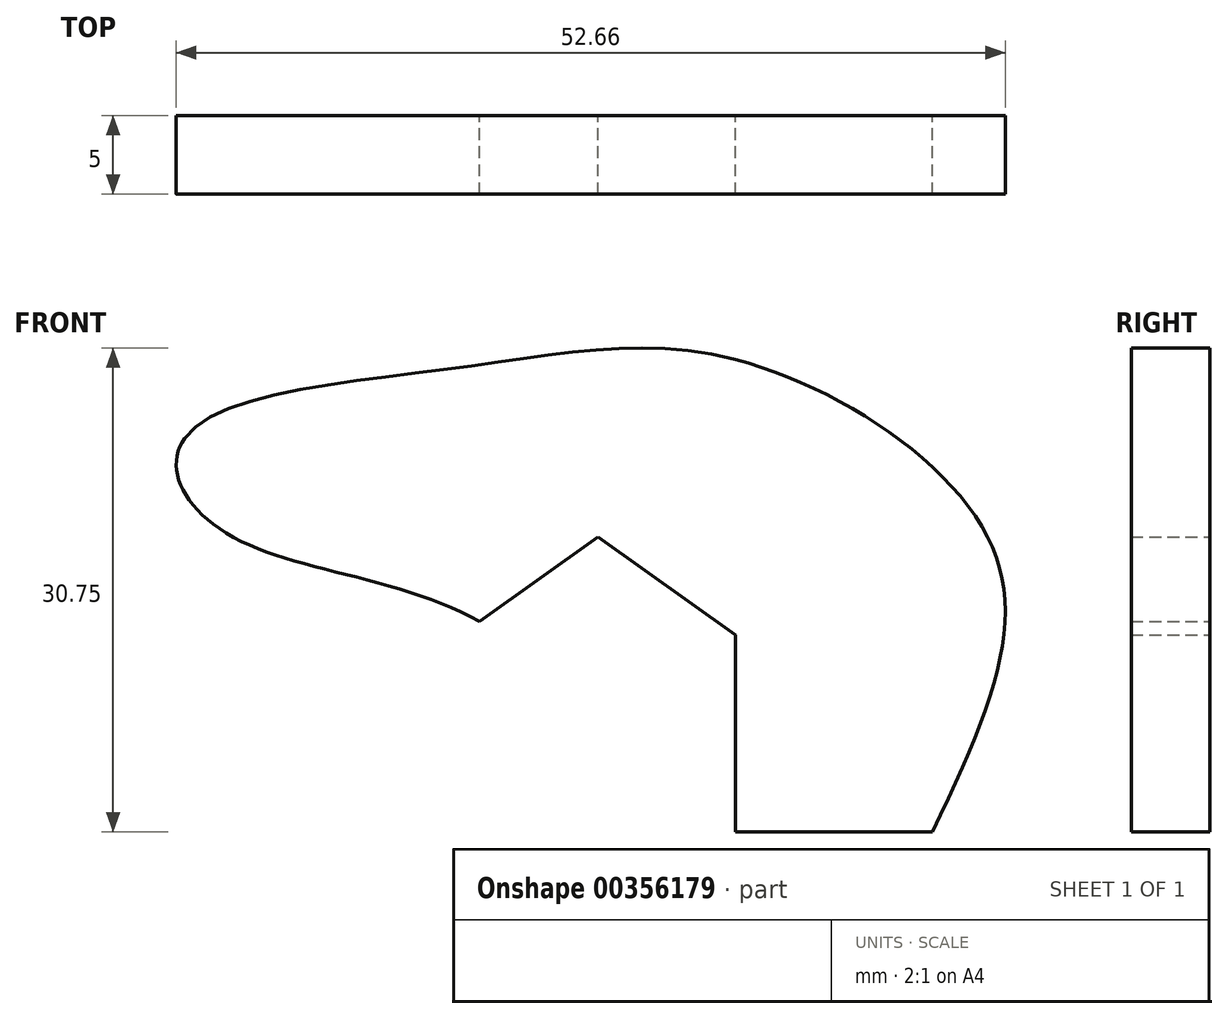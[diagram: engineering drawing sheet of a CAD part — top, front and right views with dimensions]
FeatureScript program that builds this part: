
annotation { "Feature Type Name" : "Feature", "Feature Type Description" : "" }
export const myFeature = defineFeature(function(context is Context, id is Id, definition is map)
    precondition{}
    {
        {
            var Q0;
            Q0=qCreatedBy(makeId("Front.planeOp"),FACE);
            var sketch = newSketch(context, id + "F0", { "sketchPlane" : qUnion([Q0])});
            skLineSegment(sketch, "E0", {"start": v(-12.5, 0) * mm, "end": v(12.5, 0) * mm});
            skPoint(sketch, "E1", {"position": v(0, 0) * mm});
            skLineSegment(sketch, "E2", {"start": v(0, 0) * mm, "end": v(0, 25) * mm});
            skPoint(sketch, "E3", {"position": v(0, 12.5) * mm});
            skLineSegment(sketch, "E4", {"start": v(0, 12.5) * mm, "end": v(0, 25) * mm});
            skPoint(sketch, "E5", {"position": v(0, 18.75) * mm});
            skFitSpline(sketch, "E6", {"points": [v(12.5, 0) * mm, v(16, 18.75) * mm, v(0, 30) * mm, v(-17.5, 29.5) * mm, v(-35, 25) * mm, v(-30.88, 18.22) * mm, v(-12.5, 0) * mm], "startDerivative": vector(69.6, 144.37) * mm, "endDerivative": vector(-77.1, -231.37) * mm});
            skLineSegment(sketch, "E7", {"start": v(-35, 25) * mm, "end": v(0, 25) * mm});
            skLineSegment(sketch, "E8", {"start": v(0, 18.75) * mm, "end": v(16, 18.75) * mm});
            skLineSegment(sketch, "E9", {"start": v(0, 25) * mm, "end": v(0, 30) * mm});
            skPoint(sketch, "E10", {"position": v(-17.5, 25) * mm});
            skLineSegment(sketch, "E11", {"start": v(-17.5, 25) * mm, "end": v(0, 12.5) * mm});
            skLineSegment(sketch, "E12", {"start": v(0, 25) * mm, "end": v(-8.75, 18.75) * mm});
            skLineSegment(sketch, "E13", {"start": v(0, 25) * mm, "end": v(-16.27, 13.38) * mm});
            skLineSegment(sketch, "E14", {"start": v(-35, 25) * mm, "end": v(-30.88, 18.22) * mm});
            skLineSegment(sketch, "E15", {"start": v(-17.5, 25) * mm, "end": v(-30.88, 18.22) * mm});
            skLineSegment(sketch, "E16", {"start": v(-30.88, 18.22) * mm, "end": v(-30.88, 25) * mm});
            skSolve(sketch);
        }
        {
            var Q0;
            {var subQ3=sQuery(id+"F0.wireOp",EDGE,"E2");Q0=makeQuery(id+"F0.imprint","IMPRINT",FACE,{"disambiguationData":[TD([[makeQuery(id+"F0.imprint","IMPRINT",EDGE,{"derivedFrom":subQ3}),1.0]])]});}
            var Q1;
            {var subQ0=sQuery(id+"F0.wireOp",EDGE,"E7");Q1=makeQuery(id+"F0.imprint","IMPRINT",FACE,{"disambiguationData":[TD([[makeQuery(id+"F0.imprint","IMPRINT",EDGE,{"derivedFrom":subQ0}),1.0]])]});}
            var Q2;
            {var subQ2=sQuery(id+"F0.wireOp",EDGE,"E8");Q2=makeQuery(id+"F0.imprint","IMPRINT",FACE,{"disambiguationData":[TD([[makeQuery(id+"F0.imprint","IMPRINT",EDGE,{"derivedFrom":subQ2}),1.0]])]});}
            var Q3;
            {var subQ5=sQuery(id+"F0.wireOp",EDGE,"E2");Q3=makeQuery(id+"F0.imprint","IMPRINT",FACE,{"disambiguationData":[TD([[makeQuery(id+"F0.imprint","IMPRINT",EDGE,{"derivedFrom":subQ5}),-1.0]])]});}
            var Q4;
            {var subQ0=sQuery(id+"F0.wireOp",EDGE,"E14");Q4=makeQuery(id+"F0.imprint","IMPRINT",FACE,{"disambiguationData":[TD([[makeQuery(id+"F0.imprint","IMPRINT",EDGE,{"derivedFrom":subQ0}),-1.0]])]});}
            var Q5;
            {var subQ0=sQuery(id+"F0.wireOp",EDGE,"E14");Q5=makeQuery(id+"F0.imprint","IMPRINT",FACE,{"disambiguationData":[TD([[makeQuery(id+"F0.imprint","IMPRINT",EDGE,{"derivedFrom":subQ0}),1.0]])]});}
            var Q6;
            {var subQ3=sQuery(id+"F0.wireOp",EDGE,"E15");Q6=makeQuery(id+"F0.imprint","IMPRINT",FACE,{"disambiguationData":[TD([[makeQuery(id+"F0.imprint","IMPRINT",EDGE,{"derivedFrom":subQ3}),1.0]])]});}
            var Q7;
            {var subQ0=sQuery(id+"F0.wireOp",EDGE,"E15");Q7=makeQuery(id+"F0.imprint","IMPRINT",FACE,{"disambiguationData":[TD([[makeQuery(id+"F0.imprint","IMPRINT",EDGE,{"derivedFrom":subQ0}),-1.0]])]});}
            var Q8;
            {var subQ0=sQuery(id+"F0.wireOp",EDGE,"E13");var subQ3=sQuery(id+"F0.wireOp",EDGE,"E11");var subQ5=makeQuery(id+"F0.imprint","INTERSECT",VERTEX,{"derivedFrom":[subQ3,subQ0]});Q8=makeQuery(id+"F0.imprint","IMPRINT",FACE,{"disambiguationData":[TD([[makeQuery(id+"F0.imprint","IMPRINT",EDGE,{"disambiguationData":[TD([[subQ5,1.0]])],"derivedFrom":subQ3}),1.0]])]});}
            var Q9;
            {var subQ1=sQuery(id+"F0.wireOp",EDGE,"E4");var subQ3=makeQuery(id+"F0.imprint","INTERSECT",VERTEX,{"derivedFrom":[subQ1,sQuery(id+"F0.wireOp",EDGE,"E8")]});Q9=makeQuery(id+"F0.imprint","IMPRINT",FACE,{"disambiguationData":[TD([[makeQuery(id+"F0.imprint","IMPRINT",EDGE,{"disambiguationData":[TD([[subQ3,1.0]])],"derivedFrom":subQ1}),1.0]])]});}
            extrude(context, id + "F1", {"entities" : qUnion([Q0, Q1, Q2, Q3, Q4, Q5, Q6, Q7, Q8, Q9]), "depth" : 5 * mm});
        }
    });
